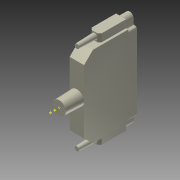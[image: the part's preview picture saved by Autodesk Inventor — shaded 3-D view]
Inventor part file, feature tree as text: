
AUTODESK INVENTOR PART (.ipt)
format: ipt  version: 2011 (Build 150239000, 239)  size: 211,456 bytes
history: native  units: in
note: dims shown in document units (in); Inventor stores cm internally (conversion verified against a paired STEP export)
features: extrude x6, sketch x6, other x4, draft x3, chamfer x2, plane x2, projected_geometry x1
ambient origin geometry x8: Origin, YZ Plane, XZ Plane, XY Plane, X Axis, Y Axis, Z Axis, Center Point
bodies: Solid1 (feature_tree)
feature tree (24):
  extrude  "Extrusion1"  Depth=1.0in TaperAngle=0.0deg
  sketch  "Sketch2"  dims[d6=0.75in d7=0.0in d8=0.0625in d9=0.125in d10=45.0deg]
  extrude  "Extrusion3"  Depth=0.0625in TaperAngle=45.0deg
  extrude  "Extrusion4"  Depth=0.25in TaperAngle=45.0deg
  chamfer  "Chamfer1"  Distance=0.5in
  extrude  "Extrusion5"  Depth=0.125in
  chamfer  "Chamfer2"  Distance=0.5in
  extrude  "Extrusion6"  Depth=0.0137in
  draft  "FaceDraft1"
  extrude  "Extrusion7"  Depth=0.0137in
  draft  "FaceDraft2"
  draft  "FaceDraft3"
  sketch  "Sketch6"  dims[d21=0.125in d22=0.5in d23=0.0in d24=0.0137in d25=0.0137in d26=0.125in d27=0.25in]
  other  "Work Point2"
  other  "Work Point3"
  sketch  "Sketch1"  dims[d0=0.243in d1=0.0in d4=1.0in d5=0.0in]
  sketch  "Sketch3"  dims[d11=0.25in d12=0.0in d13=0.25in d14=0.125in d15=45.0deg]
  sketch  "Sketch4"  dims[d16=0.375in d17=0.5in d18=0.0in]
  sketch  "Sketch5"  dims[d19=0.0137in d20=0.125in]
  projected_geometry  "Projected Loop1"
  plane  "Work Plane1"
  other  "Work Axis1"
  plane  "Work Plane2"
  other  "Work Axis2"
